# Revit family: Door-Hardware_Exit-Device_Hager_4600
name_source: partatom
category: Specialty Equipment
units: mm (PartAtom-declared; Revit-internal decimal feet)

## family parameters
Always vertical = No
Classification Number = 23.30.40.31
Cut with Voids When Loaded = No
Enable Cutting in Views = No
Maintain Annotation Orientation = No
Part Type = Normal
Room Calculation Point = No
Round Connector Dimension = Use Diameter
Shared = Yes
Work Plane-Based = Yes

## types (4) — shared parameters
Assembly Code = C1020410
Default Elevation = 0' - 0"
Keynote = 087100
Manufacturer = Hager Companies
Manufacturer Fax = 800-782-0149
Manufacturer Website = http://www.hagerco.com
Operating Temperature Range = Interior - Exterior
Product Data = http://www.arcat.com
Revision = R1_2015-10
Sales Information = http://www.hagerco.com
Specification = http://www.arcat.com
URL = http://www.hagerco.com
zero-valued in all types: Expected Lifespan (Years), Maintenance Schedule (Months), Warranty Duration (Years)

## per-type parameters (varying)
| type | Description | Model | Standards Conformance |
| Electric Rim Device Fire Rated | Hager Grade 1 Electric Exit Device - 4600 Series 4601RIMFRxxx as Specified | 4601RIMFRxxx | Grade 1  ;  BHMA ANSI 156.3  ;  Panic Hardware  ;  3 HR A Label  ;  UL 10C/B |
| Electric Rim Device Non Fire Rated | Hager Grade 1 Electric Exit Device - 4600 Series 4601RIM0xxx as Specified | 4601RIM0xxx | Grade 1  ;  BHMA ANSI 156.3  ;  Panic Hardware  ;  UL 10C/B |
| Rim Device Fire Rated | Hager Grade 1 Exit Device - 4600 Series 4601RIMFRxxx as Specified | 4601RIMFRxxx | Grade 1  ;  BHMA ANSI 156.3  ;  Panic Hardware  ;  3 HR A Label  ;  UL 10C/B |
| Rim Device Non Fire Rated | Hager Grade 1 Exit Device - 4600 Series 4601RIM0xxx as Specified | 4601RIM0xxx | Grade 1  ;  BHMA ANSI 156.3  ;  Panic Hardware  ;  UL 10C/B |

## geometry (parser evidence)
native form markers: Blend x6, Sweep x1
no freeform markers — native parametric forms only
